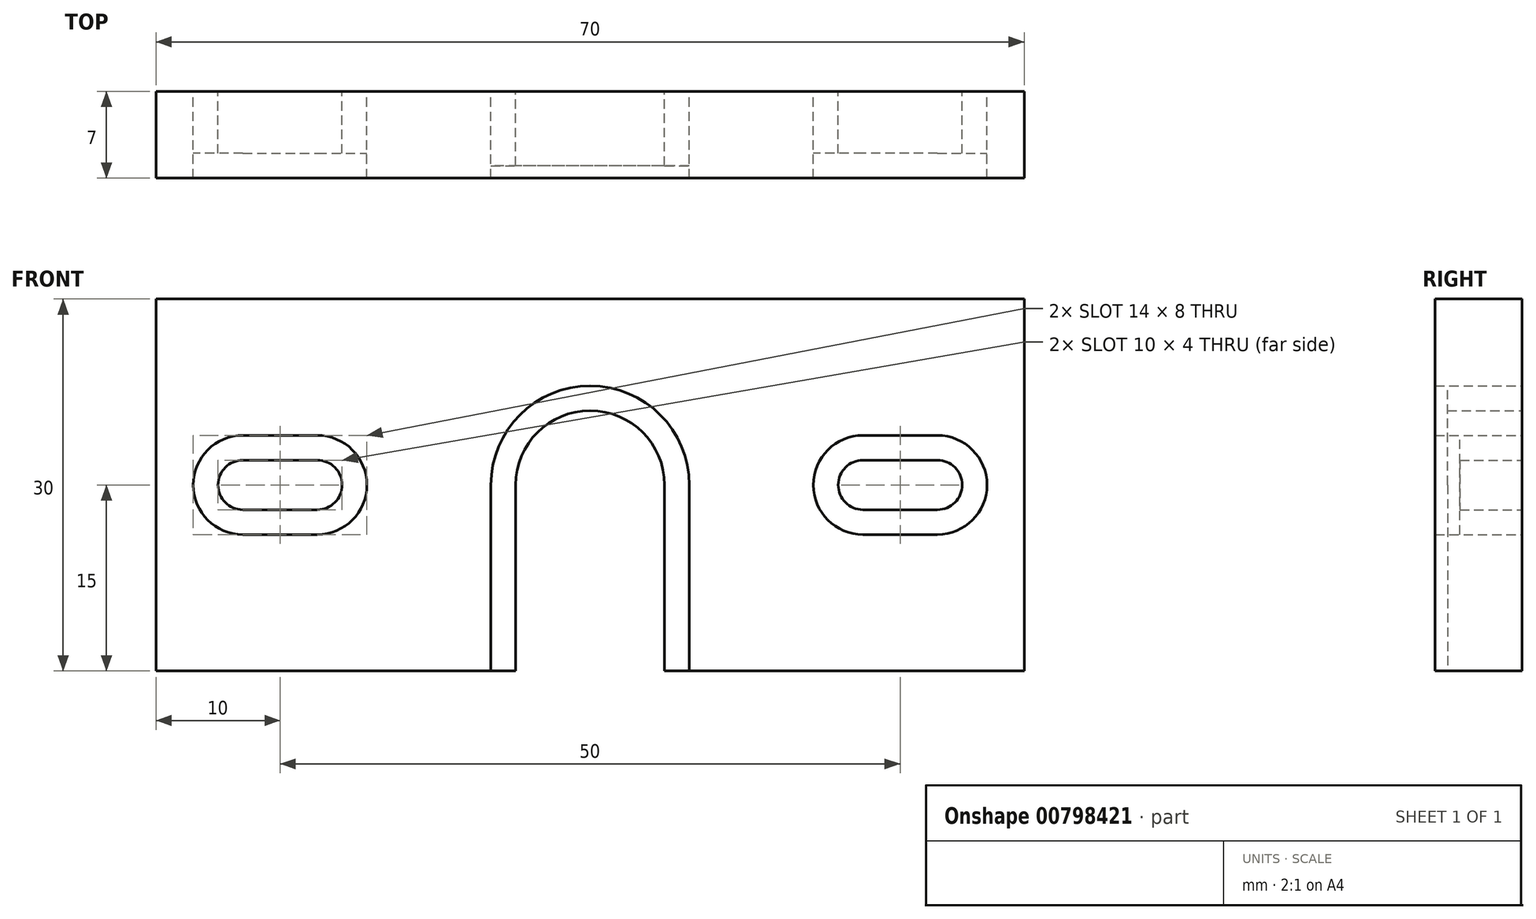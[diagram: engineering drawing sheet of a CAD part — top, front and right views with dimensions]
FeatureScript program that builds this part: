
annotation { "Feature Type Name" : "Feature", "Feature Type Description" : "" }
export const myFeature = defineFeature(function(context is Context, id is Id, definition is map)
    precondition{}
    {
        {
            var Q0;
            Q0=qCreatedBy(makeId("Front.planeOp"),FACE);
            var sketch = newSketch(context, id + "F0", { "sketchPlane" : qUnion([Q0])});
            skLineSegment(sketch, "E0.bottom", {"start": v(0, 0) * mm, "end": v(29, 0) * mm});
            skLineSegment(sketch, "E0.top", {"start": v(0, 30) * mm, "end": v(70, 30) * mm});
            skLineSegment(sketch, "E0.left", {"start": v(0, 0) * mm, "end": v(0, 30) * mm});
            skLineSegment(sketch, "E0.right", {"start": v(70, 0) * mm, "end": v(70, 30) * mm});
            skArc(sketch, "E1", {"start": v(7, 17) * mm, "mid": v(5, 15) * mm, "end": v(7, 13) * mm});
            skArc(sketch, "E2", {"start": v(13, 13) * mm, "mid": v(15, 15) * mm, "end": v(13, 17) * mm});
            skLineSegment(sketch, "E3", {"start": v(7, 17) * mm, "end": v(13, 17) * mm});
            skLineSegment(sketch, "E4", {"start": v(7, 13) * mm, "end": v(13, 13) * mm});
            skLineSegment(sketch, "E5.MirrorCS", {"start": v(63, 17) * mm, "end": v(57, 17) * mm});
            skArc(sketch, "E6", {"start": v(63, 13) * mm, "mid": v(65, 15) * mm, "end": v(63, 17) * mm});
            skArc(sketch, "E7", {"start": v(57, 17) * mm, "mid": v(55, 15) * mm, "end": v(57, 13) * mm});
            skLineSegment(sketch, "E8", {"start": v(57, 13) * mm, "end": v(63, 13) * mm});
            skArc(sketch, "E9.0", {"start": v(13, 11) * mm, "mid": v(17, 15) * mm, "end": v(13, 19) * mm});
            skLineSegment(sketch, "E10.0", {"start": v(7, 19) * mm, "end": v(13, 19) * mm});
            skArc(sketch, "E11.0", {"start": v(7, 19) * mm, "mid": v(3, 15) * mm, "end": v(7, 11) * mm});
            skLineSegment(sketch, "E12.0", {"start": v(7, 11) * mm, "end": v(13, 11) * mm});
            skLineSegment(sketch, "E13.0", {"start": v(63, 19) * mm, "end": v(57, 19) * mm});
            skArc(sketch, "E14.0", {"start": v(63, 11) * mm, "mid": v(67, 15) * mm, "end": v(63, 19) * mm});
            skLineSegment(sketch, "E15.0", {"start": v(57, 11) * mm, "end": v(63, 11) * mm});
            skArc(sketch, "E16.0", {"start": v(57, 19) * mm, "mid": v(53, 15) * mm, "end": v(57, 11) * mm});
            skArc(sketch, "E17", {"start": v(41, 15) * mm, "mid": v(35, 21) * mm, "end": v(29, 15) * mm});
            skLineSegment(sketch, "E18", {"start": v(41, 15) * mm, "end": v(41, 0) * mm});
            skLineSegment(sketch, "E19", {"start": v(29, 15) * mm, "end": v(29, 0) * mm});
            skLineSegment(sketch, "E20.trimOffspring", {"start": v(41, 0) * mm, "end": v(70, 0) * mm});
            skLineSegment(sketch, "E21.0", {"start": v(43, 15) * mm, "end": v(43, 0) * mm});
            skArc(sketch, "E22.0", {"start": v(43, 15) * mm, "mid": v(35, 23) * mm, "end": v(27, 15) * mm});
            skLineSegment(sketch, "E23.0", {"start": v(27, 15) * mm, "end": v(27, 0) * mm});
            skSolve(sketch);
        }
        {
            var Q0;
            Q0=makeQuery(id+"F0.imprint","IMPRINT",FACE,{"disambiguationData":[TD([[makeQuery(id+"F0.imprint","IMPRINT",EDGE,{"derivedFrom":sQuery(id+"F0.wireOp",EDGE,"E1")}),-1.0]])]});
            var Q1;
            Q1=makeQuery(id+"F0.imprint","IMPRINT",FACE,{"disambiguationData":[TD([[makeQuery(id+"F0.imprint","IMPRINT",EDGE,{"derivedFrom":sQuery(id+"F0.wireOp",EDGE,"E5.MirrorCS")}),-1.0]])]});
            extrude(context, id + "F1", {"entities" : qUnion([Q0, Q1]), "depth" : 5 * mm, "offsetDistance" : 25 * mm});
        }
        {
            var Q0;
            Q0=makeQuery(id+"F0.imprint","IMPRINT",FACE,{"disambiguationData":[TD([[makeQuery(id+"F0.imprint","IMPRINT",EDGE,{"derivedFrom":sQuery(id+"F0.wireOp",EDGE,"E17")}),-1.0]])]});
            extrude(context, id + "F2", {"entities" : qUnion([Q0]), "depth" : 6 * mm, "offsetDistance" : 25 * mm});
        }
        {
            var Q0;
            Q0=makeQuery(id+"F0.imprint","IMPRINT",FACE,{"disambiguationData":[TD([[makeQuery(id+"F0.imprint","IMPRINT",EDGE,{"derivedFrom":sQuery(id+"F0.wireOp",EDGE,"E0.top")}),-1.0]])]});
            extrude(context, id + "F3", {"entities" : qUnion([Q0]), "operationType" : NewBodyOperationType.ADD, "depth" : 7 * mm, "offsetDistance" : 25 * mm});
        }
        {
            var Q0;
            Q0=makeQuery(id+"F0.imprint","IMPRINT",FACE,{"disambiguationData":[TD([[makeQuery(id+"F0.imprint","IMPRINT",EDGE,{"derivedFrom":sQuery(id+"F0.wireOp",EDGE,"E0.top")}),-1.0]])]});
            extrude(context, id + "F4", {"entities" : qUnion([Q0]), "depth" : 7 * mm, "offsetDistance" : 25 * mm});
        }
    });
